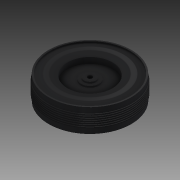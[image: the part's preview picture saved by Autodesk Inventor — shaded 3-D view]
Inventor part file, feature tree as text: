
AUTODESK INVENTOR PART (.ipt)
format: ipt  version: 2016 (Build 200138000, 138)  size: 249,856 bytes
history: native  units: mm
features: revolve x1, sketch x1
ambient origin geometry x8: Origin, YZ Plane, XZ Plane, XY Plane, X Axis, Y Axis, Z Axis, Center Point
bodies: Solid1 (feature_tree)
feature tree (2):
  revolve  "Revolution1"  [1 undecoded]
  sketch  "Sketch1"  dims[d0=15.5mm d1=3.0mm d2=12.5mm d3=7.0mm d4=5.0mm d5=13.0mm d6=11.0mm d8=3.0mm d10=4.0mm d11=13.5mm d12=26.0mm d15=90.0deg d16=3.0mm d17=2.5mm d18=1.0mm d19=2.0mm d20=1.0mm d21=33.0mm d22=3.75mm d23=3.75mm d24=0.5mm d25=0.5mm d26=0.75mm d27=0.5mm d28=0.75mm d29=0.5mm d30=0.75mm d31=0.5mm d32=0.75mm d33=0.5mm d34=0.75mm d35=0.75mm d36=1.0mm d37=1.0mm d38=12.5mm]
note: 1 required parameter value undecoded (feature->parameter linkage not recoverable at this tier; creation-order binding heuristic only, values carry confidence <= 0.55)
